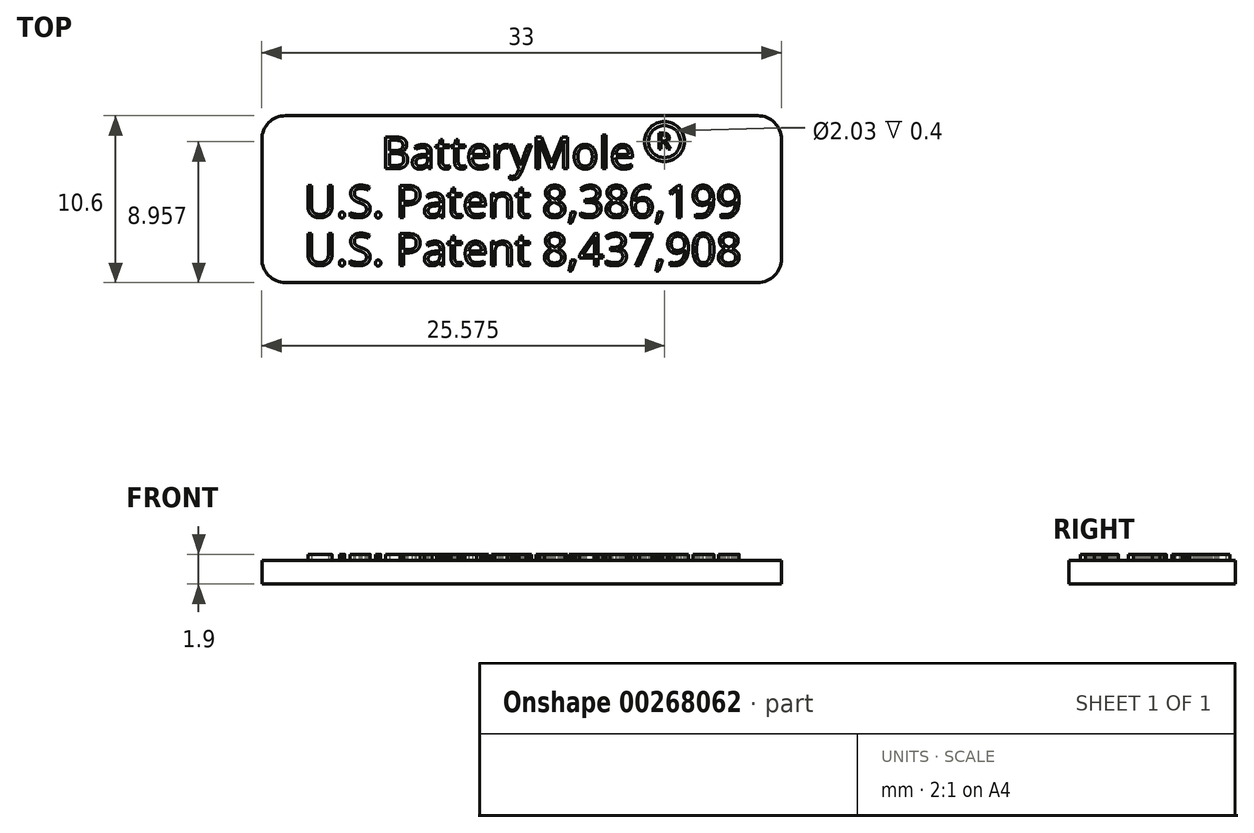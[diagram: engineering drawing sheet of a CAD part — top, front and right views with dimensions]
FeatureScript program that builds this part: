
annotation { "Feature Type Name" : "Feature", "Feature Type Description" : "" }
export const myFeature = defineFeature(function(context is Context, id is Id, definition is map)
    precondition{}
    {
        {
            var Q0;
            Q0=qCreatedBy(makeId("Top.planeOp"),FACE);
            var sketch = newSketch(context, id + "F0", { "sketchPlane" : qUnion([Q0])});
            skLineSegment(sketch, "E0.bottom", {"start": v(25, 27.12) * mm, "end": v(55, 27.12) * mm});
            skLineSegment(sketch, "E0.top", {"start": v(25, 16.52) * mm, "end": v(55, 16.52) * mm});
            skLineSegment(sketch, "E0.left", {"start": v(23.5, 25.62) * mm, "end": v(23.5, 18.02) * mm});
            skLineSegment(sketch, "E0.right", {"start": v(56.5, 25.62) * mm, "end": v(56.5, 18.02) * mm});
            skPoint(sketch, "E1.visualSharp", {"position": v(23.5, 27.12) * mm});
            skArc(sketch, "E1.filletArc", {"start": v(25, 27.12) * mm, "mid": v(23.94, 26.68) * mm, "end": v(23.5, 25.62) * mm});
            skPoint(sketch, "E2.visualSharp", {"position": v(56.5, 27.12) * mm});
            skArc(sketch, "E2.filletArc", {"start": v(56.5, 25.62) * mm, "mid": v(56.07, 26.68) * mm, "end": v(55, 27.12) * mm});
            skPoint(sketch, "E3.visualSharp", {"position": v(56.5, 16.52) * mm});
            skArc(sketch, "E3.filletArc", {"start": v(55, 16.52) * mm, "mid": v(56.07, 16.96) * mm, "end": v(56.5, 18.02) * mm});
            skPoint(sketch, "E4.visualSharp", {"position": v(23.5, 16.52) * mm});
            skArc(sketch, "E4.filletArc", {"start": v(23.5, 18.02) * mm, "mid": v(23.94, 16.96) * mm, "end": v(25, 16.52) * mm});
            skSolve(sketch);
        }
        {
            var Q0;
            Q0 = qSketchRegion(id + "F0", true);
            extrude(context, id + "F1", {"entities" : qUnion([Q0]), "depth" : 1.5 * mm});
        }
        {
            var Q0;
            Q0=makeQuery(id+"F1.opExtrude","CAP_FACE",FACE,{"disambiguationData":[OSD([sQuery(id+"F0.wireOp",EDGE,"E0.bottom"),sQuery(id+"F0.wireOp",EDGE,"E0.top"),sQuery(id+"F0.wireOp",EDGE,"E0.left"),sQuery(id+"F0.wireOp",EDGE,"E0.right"),sQuery(id+"F0.wireOp",EDGE,"E1.filletArc"),sQuery(id+"F0.wireOp",EDGE,"E2.filletArc"),sQuery(id+"F0.wireOp",EDGE,"E3.filletArc"),sQuery(id+"F0.wireOp",EDGE,"E4.filletArc")])],"isStart":false});
            var sketch = newSketch(context, id + "F2", { "sketchPlane" : qUnion([Q0])});
            skText(sketch, "E5", { "text": "BatteryMole", "fontName": "OpenSans-Regular.ttf"});
            skCircle(sketch, "E6", {"center": v(49.08, 25.48) * mm, "radius": 1.02 * mm});
            skText(sketch, "E7", { "text": "R", "fontName": "OpenSans-Regular.ttf"});
            skCircle(sketch, "E8", {"center": v(49.08, 25.48) * mm, "radius": 1.27 * mm});
            skText(sketch, "E9", { "text": "U.S. Patent 8,386,199", "fontName": "OpenSans-Regular.ttf"});
            skText(sketch, "E10", { "text": "U.S. Patent 8,437,908", "fontName": "OpenSans-Regular.ttf"});
            const initialGuessF2  = {"E5": [0.0311, 0.02376, 1, 0, 0.00203], "E7": [0.0486, 0.025, 1, 0, 0.00102], "E9": [0.02617, 0.02067, 1, 0, 0.00203], "E10": [0.02617, 0.01762, 1, 0, 0.00203]};
            skSetInitialGuess(sketch, initialGuessF2);
            skSolve(sketch);
        }
        {
            var Q0;
            Q0 = qSketchRegion(id + "F2", true);
            var Q1;
            Q1=makeQuery(id+"F2.imprint","IMPRINT",FACE,{"disambiguationData":[TD([[makeQuery(id+"F2.imprint","IMPRINT",EDGE,{"derivedFrom":sQuery(id+"F2.wireOp",EDGE,"E7.sketch_text.stroke-0")}),-1.0]])]});
            extrude(context, id + "F3", {"entities" : qUnion([Q0, Q1]), "operationType" : NewBodyOperationType.ADD, "depth" : .4 * mm});
        }
    });
